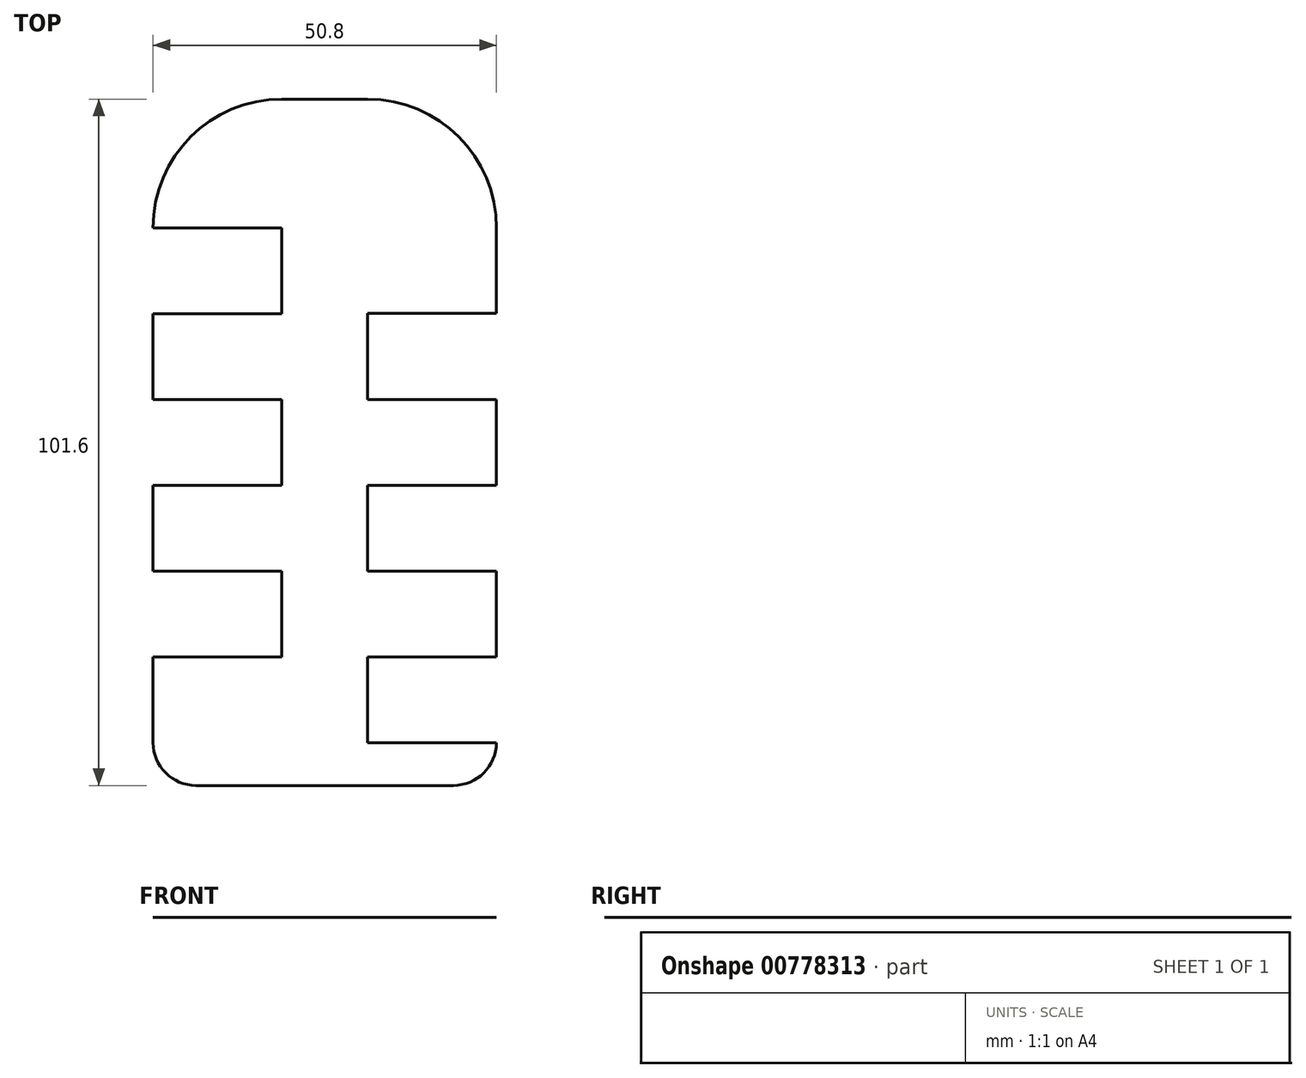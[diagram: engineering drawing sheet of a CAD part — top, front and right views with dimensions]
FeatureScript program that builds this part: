
annotation { "Feature Type Name" : "Feature", "Feature Type Description" : "" }
export const myFeature = defineFeature(function(context is Context, id is Id, definition is map)
    precondition{}
    {
        {
            var Q0;
            Q0=qCreatedBy(makeId("Top.planeOp"),FACE);
            var sketch = newSketch(context, id + "F0", { "sketchPlane" : qUnion([Q0])});
            skLineSegment(sketch, "E0.bottom", {"start": v(-6.35, 50.8) * mm, "end": v(6.35, 50.8) * mm});
            skLineSegment(sketch, "E0.top", {"start": v(-19.05, -50.8) * mm, "end": v(19.05, -50.8) * mm});
            skLineSegment(sketch, "E0.left", {"start": v(-25.4, 31.75) * mm, "end": v(-25.4, -44.45) * mm});
            skLineSegment(sketch, "E0.right", {"start": v(25.4, 31.75) * mm, "end": v(25.4, -44.45) * mm});
            skPoint(sketch, "E0.middle", {"position": v(0, 0) * mm});
            skPoint(sketch, "E1.visualSharp", {"position": v(-25.4, 50.8) * mm});
            skArc(sketch, "E1.filletArc", {"start": v(-6.35, 50.8) * mm, "mid": v(-19.82, 45.22) * mm, "end": v(-25.4, 31.75) * mm});
            skPoint(sketch, "E2.visualSharp", {"position": v(25.4, 50.8) * mm});
            skArc(sketch, "E2.filletArc", {"start": v(25.4, 31.75) * mm, "mid": v(19.82, 45.22) * mm, "end": v(6.35, 50.8) * mm});
            skLineSegment(sketch, "E3", {"start": v(-19.05, -50.8) * mm, "end": v(-19.05, -50.8) * mm});
            skLineSegment(sketch, "E4", {"start": v(19.05, -50.8) * mm, "end": v(19.05, -50.8) * mm});
            skArc(sketch, "E5.filletArc", {"start": v(-25.4, -44.45) * mm, "mid": v(-23.54, -48.94) * mm, "end": v(-19.05, -50.8) * mm});
            skArc(sketch, "E6.filletArc", {"start": v(19.05, -50.8) * mm, "mid": v(23.54, -48.94) * mm, "end": v(25.4, -44.45) * mm});
            skLineSegment(sketch, "E7", {"start": v(-25.4, 31.75) * mm, "end": v(25.4, 31.75) * mm});
            skLineSegment(sketch, "E8", {"start": v(-25.4, 31.75) * mm, "end": v(-6.35, 31.75) * mm});
            skLineSegment(sketch, "E9", {"start": v(-6.35, 31.75) * mm, "end": v(-6.35, 19.05) * mm});
            skLineSegment(sketch, "E10", {"start": v(-6.35, 19.05) * mm, "end": v(-25.4, 19.05) * mm});
            skLineSegment(sketch, "E11", {"start": v(-25.4, 19.05) * mm, "end": v(-25.4, -44.45) * mm});
            skLineSegment(sketch, "E12", {"start": v(-6.35, -44.45) * mm, "end": v(-6.35, -31.75) * mm});
            skLineSegment(sketch, "E13", {"start": v(-6.35, -31.75) * mm, "end": v(-25.4, -31.75) * mm});
            skLineSegment(sketch, "E14", {"start": v(-25.4, -31.75) * mm, "end": v(-25.4, -19.05) * mm});
            skLineSegment(sketch, "E15", {"start": v(-25.4, -19.05) * mm, "end": v(-6.35, -19.05) * mm});
            skLineSegment(sketch, "E16", {"start": v(-6.35, -19.05) * mm, "end": v(-6.35, -6.35) * mm});
            skLineSegment(sketch, "E17", {"start": v(-6.35, -6.35) * mm, "end": v(-25.4, -6.35) * mm});
            skLineSegment(sketch, "E18", {"start": v(-25.4, -6.35) * mm, "end": v(-25.4, 6.35) * mm});
            skLineSegment(sketch, "E19", {"start": v(-25.4, 6.35) * mm, "end": v(-6.35, 6.35) * mm});
            skLineSegment(sketch, "E20", {"start": v(-6.35, 6.35) * mm, "end": v(-6.35, 19.05) * mm});
            skLineSegment(sketch, "E21", {"start": v(-6.35, 6.35) * mm, "end": v(-6.35, -6.35) * mm});
            skLineSegment(sketch, "E22", {"start": v(-6.35, -19.05) * mm, "end": v(-6.35, -31.75) * mm});
            skLineSegment(sketch, "E23", {"start": v(25.4, 31.75) * mm, "end": v(6.35, 31.75) * mm});
            skLineSegment(sketch, "E24", {"start": v(6.35, 31.75) * mm, "end": v(6.35, -44.45) * mm});
            skLineSegment(sketch, "E25", {"start": v(25.4, -44.45) * mm, "end": v(6.35, -44.45) * mm});
            skLineSegment(sketch, "E26", {"start": v(25.4, -44.45) * mm, "end": v(25.4, -31.75) * mm});
            skLineSegment(sketch, "E27", {"start": v(25.4, 6.35) * mm, "end": v(25.4, -6.35) * mm});
            skLineSegment(sketch, "E28", {"start": v(25.4, -6.35) * mm, "end": v(25.4, -19.05) * mm});
            skLineSegment(sketch, "E29", {"start": v(25.4, 31.75) * mm, "end": v(25.4, 19.06) * mm});
            skLineSegment(sketch, "E30", {"start": v(25.4, 19.06) * mm, "end": v(25.4, 31.75) * mm});
            skLineSegment(sketch, "E31", {"start": v(25.4, 19.06) * mm, "end": v(6.35, 19.06) * mm});
            skLineSegment(sketch, "E32", {"start": v(25.4, 6.35) * mm, "end": v(6.35, 6.35) * mm});
            skLineSegment(sketch, "E33", {"start": v(25.4, -6.35) * mm, "end": v(6.35, -6.35) * mm});
            skLineSegment(sketch, "E34", {"start": v(25.4, -19.05) * mm, "end": v(6.35, -19.05) * mm});
            skLineSegment(sketch, "E35", {"start": v(25.4, -31.75) * mm, "end": v(6.35, -31.75) * mm});
            skSolve(sketch);
        }
        {
            var Q0;
            Q0=makeQuery(id+"F0.imprint","IMPRINT",FACE,{"disambiguationData":[TD([[makeQuery(id+"F0.imprint","IMPRINT",EDGE,{"derivedFrom":sQuery(id+"F0.wireOp",EDGE,"E0.bottom")}),-1.0]])]});
            var Q1;
            Q1=makeQuery(id+"F0.imprint","IMPRINT",FACE,{"disambiguationData":[TD([[makeQuery(id+"F0.imprint","IMPRINT",EDGE,{"derivedFrom":sQuery(id+"F0.wireOp",EDGE,"E0.top")}),1.0]])]});
            var Q2;
            {var subQ0=sQuery(id+"F0.wireOp",EDGE,"E31");Q2=makeQuery(id+"F0.imprint","IMPRINT",FACE,{"disambiguationData":[TD([[makeQuery(id+"F0.imprint","IMPRINT",EDGE,{"derivedFrom":subQ0}),-1.0]])]});}
            var Q3;
            {var subQ0=sQuery(id+"F0.wireOp",EDGE,"E32");Q3=makeQuery(id+"F0.imprint","IMPRINT",FACE,{"disambiguationData":[TD([[makeQuery(id+"F0.imprint","IMPRINT",EDGE,{"derivedFrom":subQ0}),1.0]])]});}
            var Q4;
            {var subQ0=sQuery(id+"F0.wireOp",EDGE,"E34");Q4=makeQuery(id+"F0.imprint","IMPRINT",FACE,{"disambiguationData":[TD([[makeQuery(id+"F0.imprint","IMPRINT",EDGE,{"derivedFrom":subQ0}),1.0]])]});}
            var Q5;
            {var subQ0=sQuery(id+"F0.wireOp",EDGE,"E15");Q5=makeQuery(id+"F0.imprint","IMPRINT",FACE,{"disambiguationData":[TD([[makeQuery(id+"F0.imprint","IMPRINT",EDGE,{"derivedFrom":subQ0}),1.0]])]});}
            var Q6;
            {var subQ2=sQuery(id+"F0.wireOp",EDGE,"E10");Q6=makeQuery(id+"F0.imprint","IMPRINT",FACE,{"disambiguationData":[TD([[makeQuery(id+"F0.imprint","IMPRINT",EDGE,{"derivedFrom":subQ2}),1.0]])]});}
            extrude(context, id + "F1", {"entities" : qUnion([Q0, Q1, Q2, Q3, Q4, Q5, Q6]), "depth" : 1 / 203.2 * mm, "offsetDistance" : 25.4 * mm});
        }
        {
            var Q0;
            Q0=makeQuery(id+"F1.opExtrude","SWEPT_BODY",BODY,{"disambiguationData":[OSD([sQuery(id+"F0.wireOp",EDGE,"E0.bottom"),sQuery(id+"F0.wireOp",EDGE,"E0.top"),sQuery(id+"F0.wireOp",EDGE,"E0.left"),sQuery(id+"F0.wireOp",EDGE,"E0.right"),sQuery(id+"F0.wireOp",EDGE,"E1.filletArc"),sQuery(id+"F0.wireOp",EDGE,"E2.filletArc"),sQuery(id+"F0.wireOp",EDGE,"E5.filletArc"),sQuery(id+"F0.wireOp",EDGE,"E6.filletArc"),sQuery(id+"F0.wireOp",EDGE,"E7"),sQuery(id+"F0.wireOp",EDGE,"E9"),sQuery(id+"F0.wireOp",EDGE,"E10"),sQuery(id+"F0.wireOp",EDGE,"E13"),sQuery(id+"F0.wireOp",EDGE,"E15"),sQuery(id+"F0.wireOp",EDGE,"E17"),sQuery(id+"F0.wireOp",EDGE,"E19"),sQuery(id+"F0.wireOp",EDGE,"E21"),sQuery(id+"F0.wireOp",EDGE,"E22"),sQuery(id+"F0.wireOp",EDGE,"E24"),sQuery(id+"F0.wireOp",EDGE,"E25"),sQuery(id+"F0.wireOp",EDGE,"E31"),sQuery(id+"F0.wireOp",EDGE,"E32"),sQuery(id+"F0.wireOp",EDGE,"E33"),sQuery(id+"F0.wireOp",EDGE,"E34"),sQuery(id+"F0.wireOp",EDGE,"E35")])]});
            transform(context, id + "F2", {"entities" : qUnion([Q0]), "transformType" : TransformType.TRANSLATION_3D, "dx" : 0 * mm, "dy" : 0 * mm, "dz" : 0 * mm, "makeCopy" : true});
        }
    });
